# Revit family: Door-Systems_Health-Care_TX9650SR_Single-Right-Hand-Outswing-SORH-Smoke-Rated_Tormax
name_source: partatom
category: Doors
units: mm (PartAtom-declared; Revit-internal decimal feet)

## family parameters
Always vertical = Yes
Classification Number = 23.30.10.00
Cut with Voids When Loaded = No
Host = Wall
Room Calculation Point = No
Shared = No

## types (1)
- Door-Systems_Health-Care_TX9650SR_Single-Right-Hand-Outswing-SORH-Smoke-Rated_Tormax
    Analytic Construction = <None>
    CAD Details = https://www.arcat.com
    Define Thermal Properties by = Schematic Type
    Description = Tormax Health Care Door System (HCD) - TX9650R Manual Single Outswing Door Operator - Package as Specified
    Door Frame = Alluminum
    Door Width = 3' - 6"
    Frame Projection Ext. = 0' - 1"
    Frame Projection Int. = 0' - 1"
    Frame Width = 0' - 3"
    Function = Interior
    Glass = Glass
    Handle = Stainless Steel
    Handle Height = 3' - 6"
    Height = 7' - 6"
    Keynote = 08 42 43
    Manufacturer = TORMAX USA Inc.
    Model = TX9650SR
    Product Page URL = https://www.arcat.com
    Rough Height = 7' - 8 3/16"
    Rough Width = 4' - 3 1/2"
    Specification = https://www.arcat.com
    Thickness = 0' - 1 3/4"
    URL = https://www.tormaxusa.com
    Wall Closure = By host
    Width = 4' - 0"

## geometry (parser evidence)
native form markers: Sweep x11
no freeform markers — native parametric forms only
